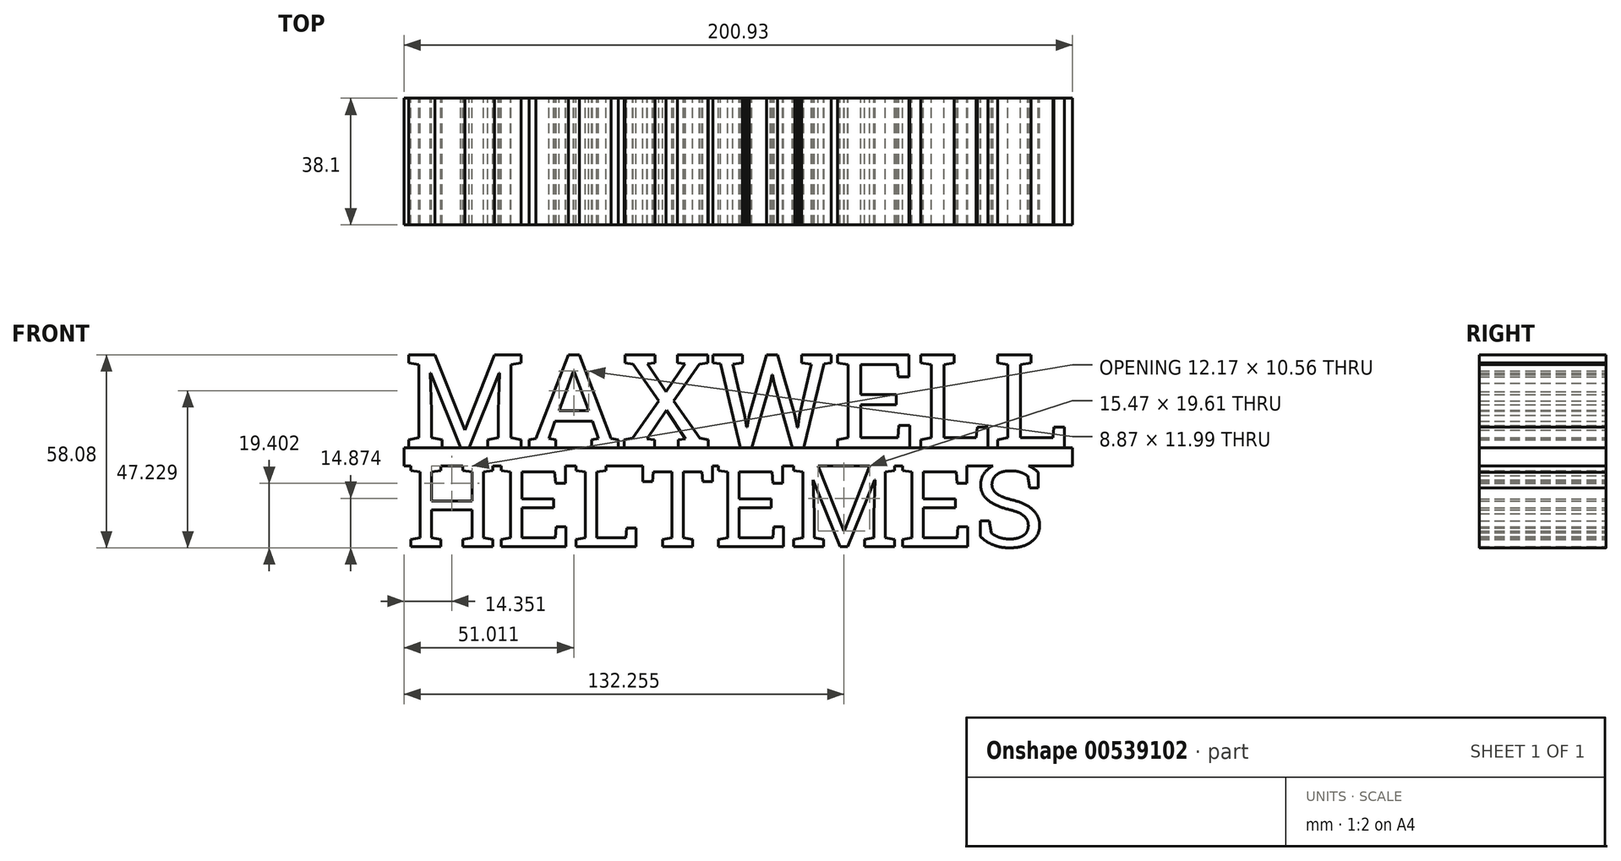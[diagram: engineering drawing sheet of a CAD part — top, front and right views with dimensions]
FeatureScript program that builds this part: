
annotation { "Feature Type Name" : "Feature", "Feature Type Description" : "" }
export const myFeature = defineFeature(function(context is Context, id is Id, definition is map)
    precondition{}
    {
        {
            var Q0;
            Q0=qCreatedBy(makeId("Front.planeOp"),FACE);
            var sketch = newSketch(context, id + "F0", { "sketchPlane" : qUnion([Q0]), "disableImprinting" : false});
            skText(sketch, "E0", { "text": "HELTEMES", "fontName": "RobotoSlab-Regular.ttf"});
            skLineSegment(sketch, "E1.bottom", {"start": v(-86.56, 24.32) * mm, "end": v(114.37, 24.32) * mm});
            skLineSegment(sketch, "E1.top", {"start": v(-86.56, 29.78) * mm, "end": v(114.37, 29.78) * mm});
            skLineSegment(sketch, "E1.left", {"start": v(-86.56, 24.32) * mm, "end": v(-86.56, 29.78) * mm});
            skLineSegment(sketch, "E1.right", {"start": v(114.37, 24.32) * mm, "end": v(114.37, 29.78) * mm});
            skText(sketch, "E2", { "text": "MAXWELL", "fontName": "RobotoSlab-Regular.ttf"});
            const initialGuessF0  = {"E0": [-0.08573, 0, 1, 0, 0.02543], "E2": [-0.08656, 0.02978, 1, 0, 0.0283]};
            skSetInitialGuess(sketch, initialGuessF0);
            skSolve(sketch);
        }
        {
            var Q0;
            Q0 = qSketchRegion(id + "F0", true);
            extrude(context, id + "F1", {"entities" : qUnion([Q0]), "depth" : 38.1 * mm, "offsetDistance" : 25.4 * mm});
        }
    });
